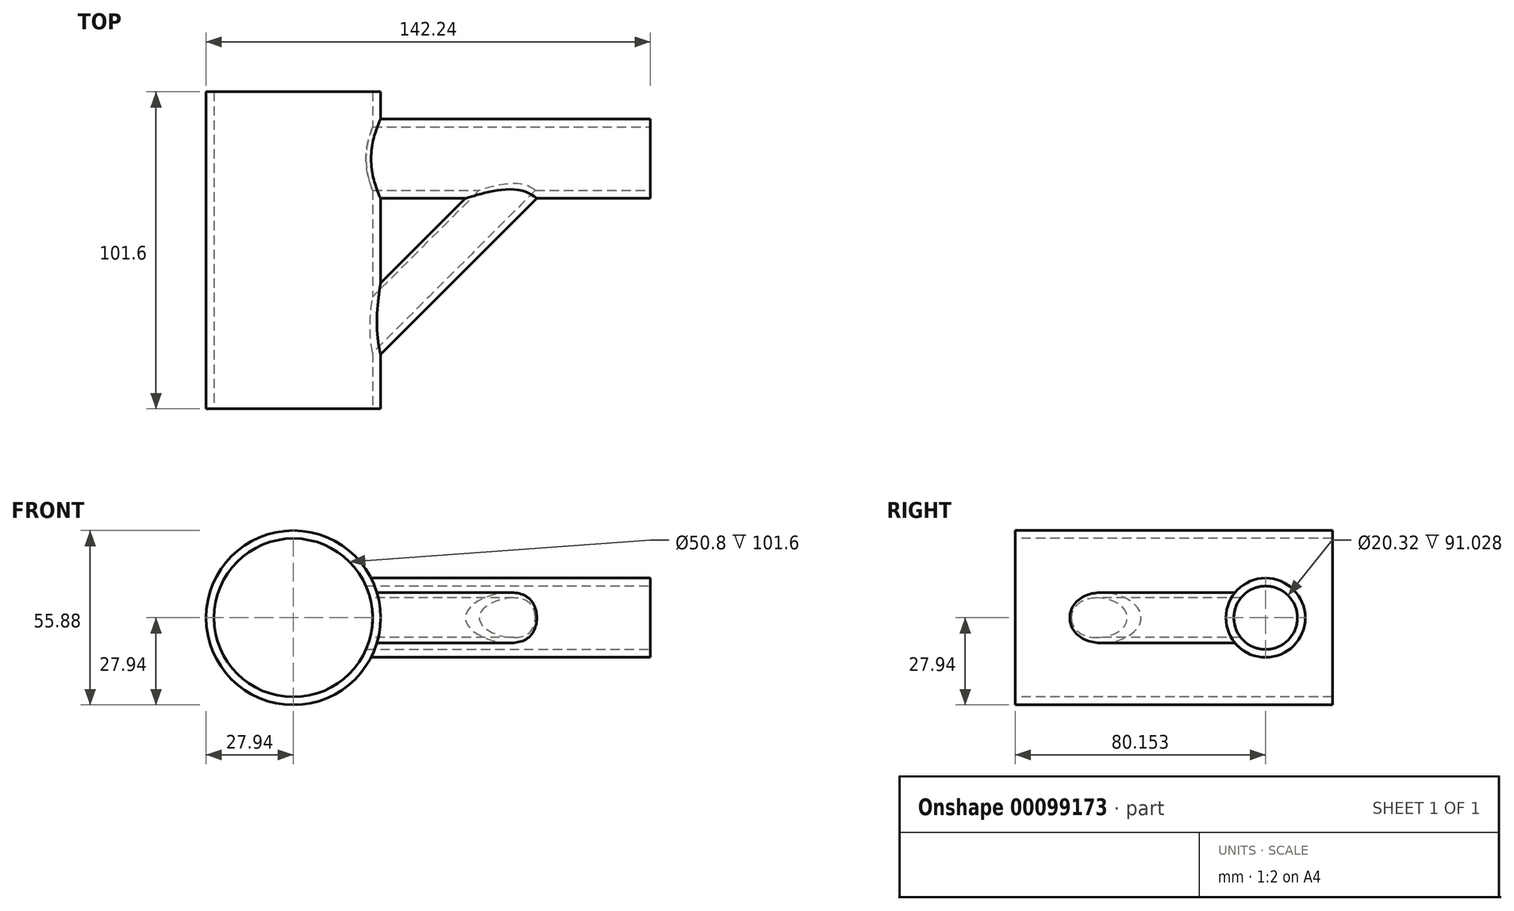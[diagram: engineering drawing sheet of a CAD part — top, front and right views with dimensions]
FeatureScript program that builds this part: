
annotation { "Feature Type Name" : "Feature", "Feature Type Description" : "" }
export const myFeature = defineFeature(function(context is Context, id is Id, definition is map)
    precondition{}
    {
        {
            var Q0;
            Q0=qCreatedBy(makeId("Front.planeOp"),FACE);
            var sketch = newSketch(context, id + "F0", { "sketchPlane" : qUnion([Q0])});
            skCircle(sketch, "E0", {"center": v(0, 0) * mm, "radius": 27.94 * mm});
            skSolve(sketch);
        }
        {
            var Q0;
            Q0 = qSketchRegion(id + "F0", true);
            extrude(context, id + "F1", {"entities" : qUnion([Q0]), "endBound" : BoundingType.SYMMETRIC, "depth" : 101.6 * mm});
        }
        {
            var Q0;
            Q0=qCreatedBy(makeId("Right.planeOp"),FACE);
            var sketch = newSketch(context, id + "F2", { "sketchPlane" : qUnion([Q0])});
            skCircle(sketch, "E1", {"center": v(29.35, 0) * mm, "radius": 12.7 * mm});
            skSolve(sketch);
        }
        {
            var Q0;
            Q0 = qSketchRegion(id + "F2", true);
            extrude(context, id + "F3", {"entities" : qUnion([Q0]), "operationType" : NewBodyOperationType.ADD, "depth" : 114.3 * mm});
        }
        {
            var Q0;
            Q0=qCreatedBy(makeId("Right.planeOp"),FACE);
            var sketch = newSketch(context, id + "F4", { "sketchPlane" : qUnion([Q0])});
            skLineSegment(sketch, "E2", {"start": v(-29.84, 40.8) * mm, "end": v(-29.84, -29.26) * mm});
            skSolve(sketch);
        }
        {
            var Q0;
            Q0 = qBodyType(qCreatedBy(id + "F4" ,EDGE), BodyType.WIRE);
            cPlane(context, id + "F5", {"entities" : qUnion([Q0]), "cplaneType" : CPlaneType.LINE_ANGLE, "offset" : 152.4 * mm, "angle" : 135 * degree, "width" : 152.4 * mm, "height" : 152.4 * mm});
        }
        {
            var Q0;
            Q0=qCreatedBy(id+"F5.planeOp",FACE);
            var sketch = newSketch(context, id + "F6", { "sketchPlane" : qUnion([Q0])});
            skCircle(sketch, "E3", {"center": v(-35.26, 0) * mm, "radius": 8.08 * mm});
            skSolve(sketch);
        }
        {
            var Q0;
            Q0 = qSketchRegion(id + "F6", true);
            extrude(context, id + "F7", {"entities" : qUnion([Q0]), "operationType" : NewBodyOperationType.ADD, "depth" : 97.33 * mm});
        }
        {
            var Q0;
            Q0=makeQuery(id+"F3.opExtrude","CAP_FACE",FACE,{"disambiguationData":[OSD([sQuery(id+"F2.wireOp",EDGE,"E1")])],"isStart":false});
            var sketch = newSketch(context, id + "F8", { "sketchPlane" : qUnion([Q0])});
            skPoint(sketch, "E4", {"position": v(29.35, 0) * mm});
            skSolve(sketch);
        }
        {
            var Q0;
            Q0=sQuery(id+"F8.wireOp",VERTEX,"E4");
            var Q1;
            Q1=makeQuery(id+"F1.opExtrude","SWEPT_BODY",BODY,{"disambiguationData":[OSD([sQuery(id+"F0.wireOp",EDGE,"E0")])]});
            hole(context, id + "F9", {"style" : HoleStyle.SIMPLE, "endStyle" : HoleEndStyle.BLIND, "holeDiameter" : 20.32 * mm, "holeDepth" : 127 * mm, "startFromSketch" : true, "locations" : qUnion([Q0]), "scope" : qUnion([Q1])});
        }
        {
            var Q0;
            Q0=makeQuery(id+"F1.opExtrude","CAP_FACE",FACE,{"disambiguationData":[OSD([sQuery(id+"F0.wireOp",EDGE,"E0")])],"isStart":false});
            var sketch = newSketch(context, id + "F10", { "sketchPlane" : qUnion([Q0])});
            skPoint(sketch, "E5", {"position": v(0, 0) * mm});
            skSolve(sketch);
        }
        {
            var Q0;
            Q0=sQuery(id+"F10.wireOp",VERTEX,"E5");
            var Q1;
            Q1=makeQuery(id+"F1.opExtrude","SWEPT_BODY",BODY,{"disambiguationData":[OSD([sQuery(id+"F0.wireOp",EDGE,"E0")])]});
            hole(context, id + "F11", {"style" : HoleStyle.SIMPLE, "endStyle" : HoleEndStyle.BLIND, "holeDiameter" : 50.8 * mm, "holeDepth" : 127 * mm, "startFromSketch" : true, "locations" : qUnion([Q0]), "scope" : qUnion([Q1])});
        }
        {
            var Q0;
            Q0=qCreatedBy(id+"F5.planeOp",FACE);
            var sketch = newSketch(context, id + "F12", { "sketchPlane" : qUnion([Q0])});
            skPoint(sketch, "E6", {"position": v(-34.84, 0) * mm});
            skSolve(sketch);
        }
        {
            var Q0;
            Q0=sQuery(id+"F12.wireOp",VERTEX,"E6");
            var Q1;
            Q1=makeQuery(id+"F1.opExtrude","SWEPT_BODY",BODY,{"disambiguationData":[OSD([sQuery(id+"F0.wireOp",EDGE,"E0")])]});
            hole(context, id + "F13", {"style" : HoleStyle.SIMPLE, "endStyle" : HoleEndStyle.BLIND, "oppositeDirection" : true, "holeDiameter" : 12.7 * mm, "holeDepth" : 93.98 * mm, "startFromSketch" : true, "locations" : qUnion([Q0]), "scope" : qUnion([Q1])});
        }
    });
